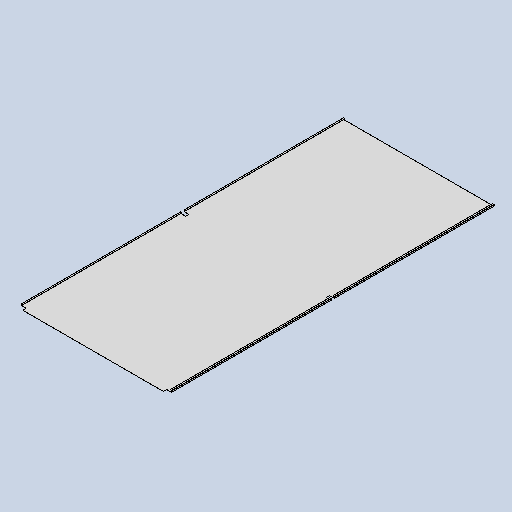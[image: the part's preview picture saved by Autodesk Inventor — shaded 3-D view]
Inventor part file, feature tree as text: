
AUTODESK INVENTOR PART (.ipt)
format: ipt  version: 2025 (Build 290162010, 162A)  size: 281,600 bytes
history: native  units: mm
features: sheet_metal_op x7, sketch x4, other x4, extrude x1, chamfer x1, projected_geometry x1
ambient origin geometry x8: Origin, YZ Plane, XZ Plane, XY Plane, X Axis, Y Axis, Z Axis, Center Point
bodies: Body1 (feature_tree)
feature tree (18):
  sheet_metal_op  "Face1"
  sheet_metal_op  "Flange1"
  sheet_metal_op  "Flange2"
  extrude  "Extrusion3"  Depth=915.0mm
  chamfer  "Corner Round1"
  sketch  "Sketch6"  dims[d12=23.212879mm d52=915.0mm]
  other  "Plate2"
  sketch  "Sketch10"  dims[d53=1980.0mm]
  other  "Plate3"
  sheet_metal_op  "Bend2"
  sheet_metal_op  "Corner2"
  sketch  "Sketch11"  dims[d54=0.5mm]
  other  "Plate4"
  sheet_metal_op  "Bend3"
  sheet_metal_op  "Corner3"
  sketch  "Sketch12"  dims[d74=0.5mm d75=0.25mm d76=1.0mm d77=0.5mm d78=10.0mm d79=90.0deg d80=0.5mm d81=2.0mm d82=0.5mm d83=0.5mm d84=0.5mm d85=0.25mm d86=1.0mm d87=0.5mm d88=10.0mm d89=90.0deg d90=0.5mm d91=2.0mm d92=0.5mm d93=0.5mm d94=0.0mm d95=0.0mm d96=20.0mm d97=30.0mm d109=990.0mm d110=30.0mm d111=4.0mm]
  projected_geometry  "Projected Loop5"
  other  "Definition1"
